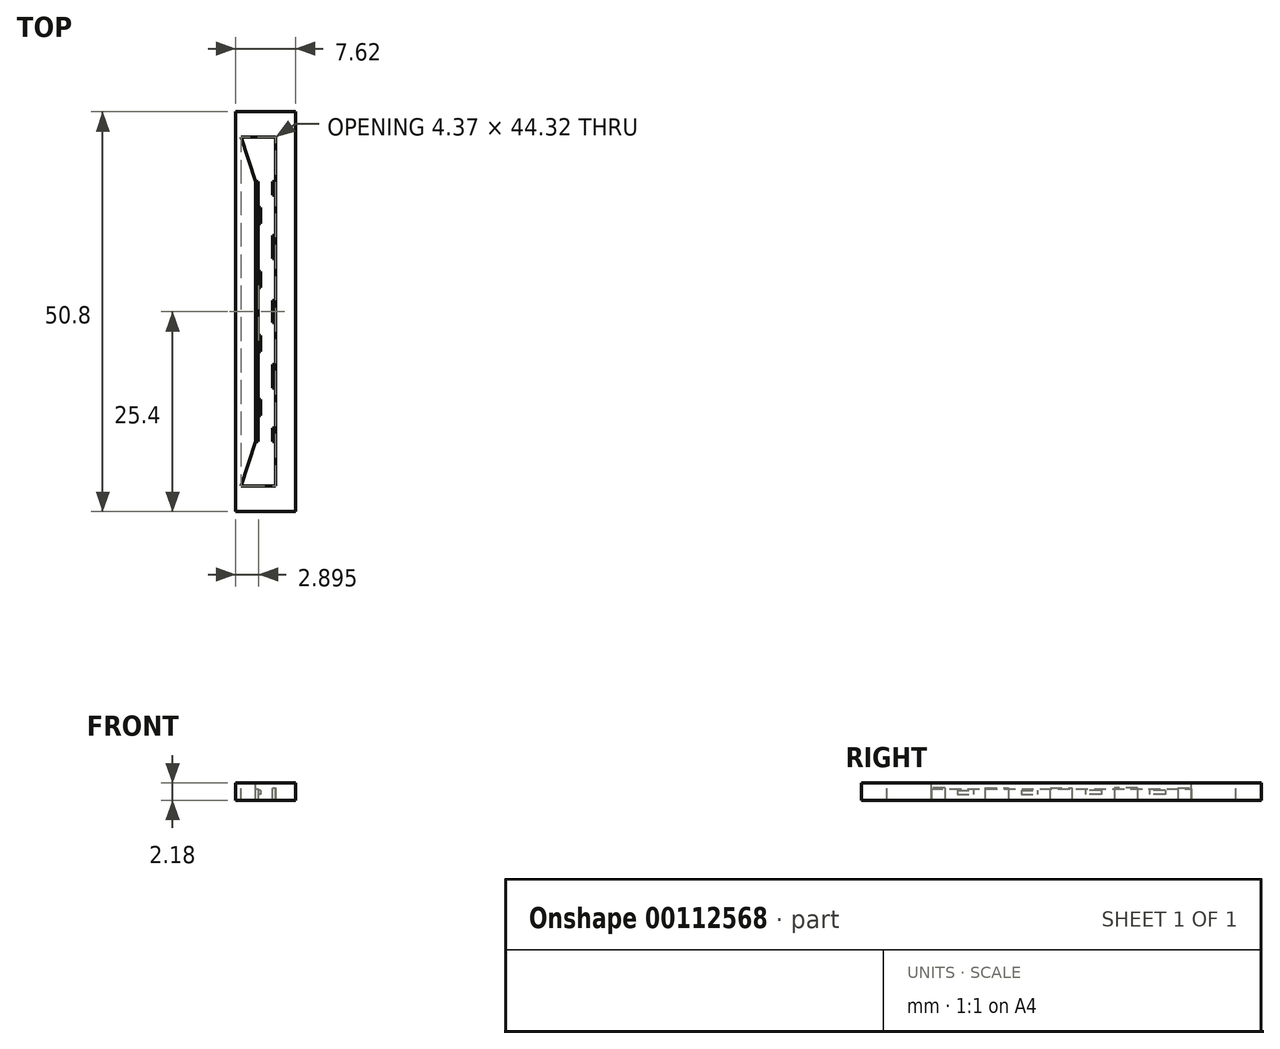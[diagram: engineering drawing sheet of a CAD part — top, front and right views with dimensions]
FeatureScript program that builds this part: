
annotation { "Feature Type Name" : "Feature", "Feature Type Description" : "" }
export const myFeature = defineFeature(function(context is Context, id is Id, definition is map)
    precondition{}
    {
        {
            var Q0;
            Q0=qCreatedBy(makeId("Top.planeOp"),FACE);
            var sketch = newSketch(context, id + "F0", { "sketchPlane" : qUnion([Q0])});
            skLineSegment(sketch, "E0.bottom", {"start": v(3.81, -25.4) * mm, "end": v(-3.81, -25.4) * mm});
            skLineSegment(sketch, "E0.top", {"start": v(3.81, 25.4) * mm, "end": v(-3.81, 25.4) * mm});
            skLineSegment(sketch, "E0.left", {"start": v(3.8, -25.4) * mm, "end": v(3.81, 25.4) * mm});
            skLineSegment(sketch, "E0.right", {"start": v(-3.81, -25.4) * mm, "end": v(-3.81, 25.4) * mm});
            skPoint(sketch, "E0.middle", {"position": v(0, 0) * mm});
            skSolve(sketch);
        }
        {
            var Q0;
            Q0=makeQuery(id+"F0.imprint","IMPRINT",FACE,{"disambiguationData":[TD([[makeQuery(id+"F0.imprint","IMPRINT",EDGE,{"derivedFrom":sQuery(id+"F0.wireOp",EDGE,"E0.bottom")}),-1.0]])]});
            extrude(context, id + "F1", {"entities" : qUnion([Q0]), "depth" : 2.18 * mm});
        }
        {
            var Q0;
            Q0=qCreatedBy(makeId("Front.planeOp"),FACE);
            var sketch = newSketch(context, id + "F2", { "sketchPlane" : qUnion([Q0])});
            skLineSegment(sketch, "E1.bottom", {"start": v(1.27, 0) * mm, "end": v(-0.97, 0) * mm});
            skLineSegment(sketch, "E1.top", {"start": v(1.27, 2.18) * mm, "end": v(-1.27, 2.18) * mm});
            skLineSegment(sketch, "E1.left", {"start": v(1.27, 0) * mm, "end": v(1.27, 2.18) * mm});
            skLineSegment(sketch, "E1.right", {"start": v(-1.27, 1.47) * mm, "end": v(-1.27, 2.18) * mm});
            skPoint(sketch, "E1.middle", {"position": v(0, 1.1) * mm});
            skLineSegment(sketch, "E2", {"start": v(-1.27, 1.47) * mm, "end": v(-0.97, 1.47) * mm});
            skLineSegment(sketch, "E3", {"start": v(-0.97, 1.47) * mm, "end": v(-0.97, 0) * mm});
            skPoint(sketch, "E4.orphan", {"position": v(-1.27, 0) * mm});
            skSolve(sketch);
        }
        {
            var Q0;
            Q0 = qSketchRegion(id + "F2", true);
            extrude(context, id + "F3", {"entities" : qUnion([Q0]), "operationType" : NewBodyOperationType.REMOVE, "endBound" : BoundingType.SYMMETRIC, "depth" : 33.02 * mm});
        }
        {
            var Q0;
            Q0=makeQuery(id+"F3.boolean.opBoolean","COPY",FACE,{"derivedFrom":makeQuery(id+"F3.opExtrude","SWEPT_FACE",FACE,{"disambiguationData":[OSD([sQuery(id+"F2.wireOp",EDGE,"E1.left")])]})});
            var sketch = newSketch(context, id + "F4", { "sketchPlane" : qUnion([Q0])});
            skLineSegment(sketch, "E5.bottom", {"start": v(1.4, 0) * mm, "end": v(-1.4, 0) * mm});
            skLineSegment(sketch, "E5.top", {"start": v(1.4, 1.57) * mm, "end": v(-1.4, 1.57) * mm});
            skLineSegment(sketch, "E5.left", {"start": v(1.4, 0) * mm, "end": v(1.4, 1.57) * mm});
            skLineSegment(sketch, "E5.right", {"start": v(-1.4, 0) * mm, "end": v(-1.4, 1.57) * mm});
            skPoint(sketch, "E5.middle", {"position": v(0, 0.79) * mm});
            skLineSegment(sketch, "E6", {"start": v(0, 5.78) * mm, "end": v(0, -5.42) * mm, "construction": true});
            skLineSegment(sketch, "E7", {"start": v(-25.4, 1.57) * mm, "end": v(25.4, 1.57) * mm, "construction": true});
            skLineSegment(sketch, "E8.bottom", {"start": v(-9.68, 1.57) * mm, "end": v(-6.73, 1.57) * mm});
            skLineSegment(sketch, "E8.top", {"start": v(-9.68, 0) * mm, "end": v(-6.73, 0) * mm});
            skLineSegment(sketch, "E8.left", {"start": v(-9.68, 1.57) * mm, "end": v(-9.68, 0) * mm});
            skLineSegment(sketch, "E8.right", {"start": v(-6.73, 1.57) * mm, "end": v(-6.73, 0) * mm});
            skLineSegment(sketch, "E9.MirrorCS", {"start": v(9.68, 1.57) * mm, "end": v(9.68, 0) * mm});
            skLineSegment(sketch, "E10.MirrorCS", {"start": v(25.4, 1.57) * mm, "end": v(-25.4, 1.57) * mm, "construction": true});
            skLineSegment(sketch, "E11.MirrorCS", {"start": v(6.73, 1.57) * mm, "end": v(6.73, 0) * mm});
            skLineSegment(sketch, "E12.MirrorCS", {"start": v(9.68, 0) * mm, "end": v(6.73, 0) * mm});
            skLineSegment(sketch, "E13.MirrorCS", {"start": v(9.68, 1.57) * mm, "end": v(6.73, 1.57) * mm});
            skLineSegment(sketch, "E14.bottom", {"start": v(-14.78, 1.57) * mm, "end": v(-16.51, 1.57) * mm});
            skLineSegment(sketch, "E14.top", {"start": v(-14.78, 0) * mm, "end": v(-16.51, 0) * mm});
            skLineSegment(sketch, "E14.left", {"start": v(-14.78, 1.57) * mm, "end": v(-14.78, 0) * mm});
            skLineSegment(sketch, "E14.right", {"start": v(-16.51, 1.57) * mm, "end": v(-16.51, 0) * mm});
            skLineSegment(sketch, "E15.MirrorCS", {"start": v(14.78, 1.57) * mm, "end": v(16.51, 1.57) * mm});
            skLineSegment(sketch, "E16.MirrorCS", {"start": v(14.78, 1.57) * mm, "end": v(14.78, 0) * mm});
            skLineSegment(sketch, "E17.MirrorCS", {"start": v(14.78, 0) * mm, "end": v(16.51, 0) * mm});
            skLineSegment(sketch, "E18.MirrorCS", {"start": v(16.51, 1.57) * mm, "end": v(16.51, 0) * mm});
            skSolve(sketch);
        }
        {
            var Q0;
            Q0 = qSketchRegion(id + "F4", true);
            extrude(context, id + "F5", {"entities" : qUnion([Q0]), "operationType" : NewBodyOperationType.ADD, "depth" : 0.37 * mm});
        }
        {
            var Q0;
            Q0=makeQuery(id+"F3.boolean.opBoolean","COPY",FACE,{"derivedFrom":makeQuery(id+"F3.opExtrude","SWEPT_FACE",FACE,{"disambiguationData":[OSD([sQuery(id+"F2.wireOp",EDGE,"E3")])]})});
            var sketch = newSketch(context, id + "F6", { "sketchPlane" : qUnion([Q0])});
            skLineSegment(sketch, "E19", {"start": v(0, 2.28) * mm, "end": v(0, 0) * mm, "construction": true});
            skLineSegment(sketch, "E20", {"start": v(-25.4, 1.27) * mm, "end": v(25.4, 1.27) * mm, "construction": true});
            skLineSegment(sketch, "E21", {"start": v(-25.4, 0.76) * mm, "end": v(25.4, 0.76) * mm, "construction": true});
            skLineSegment(sketch, "E22.bottom", {"start": v(-5.08, 1.27) * mm, "end": v(-3.05, 1.27) * mm});
            skLineSegment(sketch, "E22.top", {"start": v(-5.08, 0.76) * mm, "end": v(-3.05, 0.76) * mm});
            skLineSegment(sketch, "E22.left", {"start": v(-5.08, 1.27) * mm, "end": v(-5.08, 0.76) * mm});
            skLineSegment(sketch, "E22.right", {"start": v(-3.05, 1.27) * mm, "end": v(-3.05, 0.76) * mm});
            skLineSegment(sketch, "E23.MirrorCS", {"start": v(3.05, 1.27) * mm, "end": v(3.05, 0.76) * mm});
            skLineSegment(sketch, "E24.MirrorCS", {"start": v(5.08, 1.27) * mm, "end": v(5.08, 0.76) * mm});
            skLineSegment(sketch, "E25.MirrorCS", {"start": v(5.08, 0.76) * mm, "end": v(3.05, 0.76) * mm});
            skLineSegment(sketch, "E26.MirrorCS", {"start": v(5.08, 1.27) * mm, "end": v(3.05, 1.27) * mm});
            skLineSegment(sketch, "E27.bottom", {"start": v(-13.2, 1.27) * mm, "end": v(-11.18, 1.27) * mm});
            skLineSegment(sketch, "E27.top", {"start": v(-13.2, 0.76) * mm, "end": v(-11.18, 0.76) * mm});
            skLineSegment(sketch, "E27.left", {"start": v(-13.2, 1.27) * mm, "end": v(-13.2, 0.76) * mm});
            skLineSegment(sketch, "E27.right", {"start": v(-11.18, 1.27) * mm, "end": v(-11.18, 0.76) * mm});
            skLineSegment(sketch, "E28.MirrorCS", {"start": v(11.18, 1.27) * mm, "end": v(11.18, 0.76) * mm});
            skLineSegment(sketch, "E29.MirrorCS", {"start": v(13.2, 1.27) * mm, "end": v(13.2, 0.76) * mm});
            skLineSegment(sketch, "E30.MirrorCS", {"start": v(13.2, 1.27) * mm, "end": v(11.18, 1.27) * mm});
            skLineSegment(sketch, "E31.MirrorCS", {"start": v(13.2, 0.76) * mm, "end": v(11.18, 0.76) * mm});
            skSolve(sketch);
        }
        {
            var Q0;
            Q0 = qSketchRegion(id + "F6", true);
            extrude(context, id + "F7", {"entities" : qUnion([Q0]), "operationType" : NewBodyOperationType.ADD, "depth" : 0.33 * mm});
        }
        {
            var Q0;
            Q0=makeQuery(id+"F1.opExtrude","CAP_FACE",FACE,{"disambiguationData":[OSD([sQuery(id+"F0.wireOp",EDGE,"E0.bottom"),sQuery(id+"F0.wireOp",EDGE,"E0.top"),sQuery(id+"F0.wireOp",EDGE,"E0.left"),sQuery(id+"F0.wireOp",EDGE,"E0.right")])],"isStart":false});
            var sketch = newSketch(context, id + "F8", { "sketchPlane" : qUnion([Q0])});
            skLineSegment(sketch, "E32", {"start": v(6, 0) * mm, "end": v(-8.25, 0) * mm, "construction": true});
            skPoint(sketch, "E32.endSnap0", {"position": v(3.81, 0) * mm});
            skLineSegment(sketch, "E33", {"start": v(-1.27, 16.51) * mm, "end": v(-3.1, 22.16) * mm});
            skLineSegment(sketch, "E34", {"start": v(-3.1, 22.16) * mm, "end": v(1.27, 22.16) * mm});
            skLineSegment(sketch, "E35", {"start": v(1.27, 22.16) * mm, "end": v(1.27, 16.51) * mm});
            skLineSegment(sketch, "E36", {"start": v(1.27, 16.51) * mm, "end": v(-1.27, 16.51) * mm});
            skLineSegment(sketch, "E37.MirrorCS", {"start": v(-1.27, -16.51) * mm, "end": v(-3.1, -22.16) * mm});
            skLineSegment(sketch, "E38.MirrorCS", {"start": v(-3.1, -22.16) * mm, "end": v(1.27, -22.16) * mm});
            skLineSegment(sketch, "E39.MirrorCS", {"start": v(1.27, -22.16) * mm, "end": v(1.27, -16.51) * mm});
            skLineSegment(sketch, "E40.MirrorCS", {"start": v(1.27, -16.51) * mm, "end": v(-1.27, -16.51) * mm});
            skSolve(sketch);
        }
        {
            var Q0;
            Q0 = qSketchRegion(id + "F8", true);
            extrude(context, id + "F9", {"entities" : qUnion([Q0]), "operationType" : NewBodyOperationType.REMOVE, "oppositeDirection" : true, "depth" : 25.4 * mm});
        }
        {
            var Q0;
            Q0=makeQuery(id+"F1.opExtrude","SWEPT_BODY",BODY,{"disambiguationData":[OSD([sQuery(id+"F0.wireOp",EDGE,"E0.bottom"),sQuery(id+"F0.wireOp",EDGE,"E0.top"),sQuery(id+"F0.wireOp",EDGE,"E0.left"),sQuery(id+"F0.wireOp",EDGE,"E0.right")])]});
            transform(context, id + "F10", {"entities" : qUnion([Q0]), "transformType" : TransformType.TRANSLATION_3D, "dx" : 7.62 * mm, "dy" : 0 * mm, "dz" : 0 * mm, "makeCopy" : true});
        }
        {
            var Q0;
            Q0=makeQuery(id+"F10.opPattern","COPY",BODY,{"derivedFrom":makeQuery(id+"F1.opExtrude","SWEPT_BODY",BODY,{"disambiguationData":[OSD([sQuery(id+"F0.wireOp",EDGE,"E0.bottom"),sQuery(id+"F0.wireOp",EDGE,"E0.top"),sQuery(id+"F0.wireOp",EDGE,"E0.left"),sQuery(id+"F0.wireOp",EDGE,"E0.right")])]}),"instanceName":"1"});
            transform(context, id + "F11", {"entities" : qUnion([Q0]), "transformType" : TransformType.TRANSLATION_3D, "dx" : 7.62 * mm, "dy" : 0 * mm, "dz" : 0 * mm, "makeCopy" : true});
        }
        {
            var Q0;
            Q0=makeQuery(id+"F11.opPattern","COPY",BODY,{"derivedFrom":makeQuery(id+"F10.opPattern","COPY",BODY,{"derivedFrom":makeQuery(id+"F1.opExtrude","SWEPT_BODY",BODY,{"disambiguationData":[OSD([sQuery(id+"F0.wireOp",EDGE,"E0.bottom"),sQuery(id+"F0.wireOp",EDGE,"E0.top"),sQuery(id+"F0.wireOp",EDGE,"E0.left"),sQuery(id+"F0.wireOp",EDGE,"E0.right")])]}),"instanceName":"1"}),"instanceName":"1"});
            transform(context, id + "F12", {"entities" : qUnion([Q0]), "transformType" : TransformType.TRANSLATION_3D, "dx" : 7.62 * mm, "dy" : 0 * mm, "dz" : 0 * mm, "makeCopy" : true});
        }
        {
            var Q0;
            Q0=makeQuery(id+"F12.opPattern","COPY",BODY,{"derivedFrom":makeQuery(id+"F11.opPattern","COPY",BODY,{"derivedFrom":makeQuery(id+"F10.opPattern","COPY",BODY,{"derivedFrom":makeQuery(id+"F1.opExtrude","SWEPT_BODY",BODY,{"disambiguationData":[OSD([sQuery(id+"F0.wireOp",EDGE,"E0.bottom"),sQuery(id+"F0.wireOp",EDGE,"E0.top"),sQuery(id+"F0.wireOp",EDGE,"E0.left"),sQuery(id+"F0.wireOp",EDGE,"E0.right")])]}),"instanceName":"1"}),"instanceName":"1"}),"instanceName":"1"});
            var Q1;
            Q1=makeQuery(id+"F11.opPattern","COPY",BODY,{"derivedFrom":makeQuery(id+"F10.opPattern","COPY",BODY,{"derivedFrom":makeQuery(id+"F1.opExtrude","SWEPT_BODY",BODY,{"disambiguationData":[OSD([sQuery(id+"F0.wireOp",EDGE,"E0.bottom"),sQuery(id+"F0.wireOp",EDGE,"E0.top"),sQuery(id+"F0.wireOp",EDGE,"E0.left"),sQuery(id+"F0.wireOp",EDGE,"E0.right")])]}),"instanceName":"1"}),"instanceName":"1"});
            deleteBodies(context, id + "F13", {"entities" : qUnion([Q0, Q1])});
        }
        {
            var Q0;
            Q0=makeQuery(id+"F10.opPattern","COPY",BODY,{"derivedFrom":makeQuery(id+"F1.opExtrude","SWEPT_BODY",BODY,{"disambiguationData":[OSD([sQuery(id+"F0.wireOp",EDGE,"E0.bottom"),sQuery(id+"F0.wireOp",EDGE,"E0.top"),sQuery(id+"F0.wireOp",EDGE,"E0.left"),sQuery(id+"F0.wireOp",EDGE,"E0.right")])]}),"instanceName":"1"});
            deleteBodies(context, id + "F14", {"entities" : qUnion([Q0])});
        }
    });
